# Revit family: Artek_Lounge Chairs_Kiki Lounge Chair_Kiki Lounge Chair
name_source: partatom
category: Furniture
revit_build: Autodesk Revit 2018 (Build: 20170223_1515(x64)
units: mm (PartAtom-declared; Revit-internal decimal feet)

## family parameters
Always vertical = Yes
Cut with Voids When Loaded = No
OmniClass Number = 23.40.20.14.14.11
OmniClass Title = Chairs
Room Calculation Point = No
Shared = No
Work Plane-Based = No

## types (1)
- Kiki Lounge Chair
    AssetType = Movable
    BIMObjectName = Artek_Lounge Chairs_Kiki Lounge Chair_Kiki Lounge Chair
    Brand = Artek
    Category = Lounge Chairs
    Collection = Kiki Collection
    Color = Black
    ConvergoRefNr = 0190-2009-0047-FI
    Cost = 0 $
    Description = The Kiki Lounge Chair has a frame made of distinctive oval steel tubing. The upholstery offers clean, smooth-edged contours that provide comfort and support.
    Designer = Ilmari Tapiovaara
    DurationUnit = Years
    HighestSeatingHeight = 413 mm
    IfcExportAs = IfcFurnishingElementType
    IfcExportType = CHAIR
    LoungeChairMainMaterial = Canola
    LoungeChairSecondaryMaterial = Powder coated black metal
    LowestSeatingHeight = 413 mm
    MainColor = Black
    Manufacturer = Artek
    ManufacturerName = Artek
    ManufacturerURL = https://www.artek.fi
    Material = Steel tubing/Upholstery
    Model = Kiki Lounge Chair
    ModelNumber = 28201302
    NBSDescription = Domestic chairs
    NBSReference = 45-35-20/365
    Name = Kiki Lounge Chair
    NominalDepth = 714 mm
    NominalHeight = 703 mm
    NominalLength = 603 mm
    ProductInformation = The Kiki Lounge Chair has a frame made of distinctive oval steel tubing. The upholstery offers clean, smooth-edged contours that provide comfort and support.
    SeatingHeight = 413 mm
    Shape = Sculptured
    Size = 600x680x750 mm
    URL = https://www.artek.fi
    Uniclass2 = Pr_40_50_12_48
    Uniclass2015Description = Lounge chairs
    Uniclass2015Reference = Pr_40_50_12_48
    Version = 1
    VersionDate = 11/3/2020
    WarrantyDurationUnit = Years

## geometry (parser evidence)
native form markers: Sweep x5
no freeform markers — native parametric forms only
